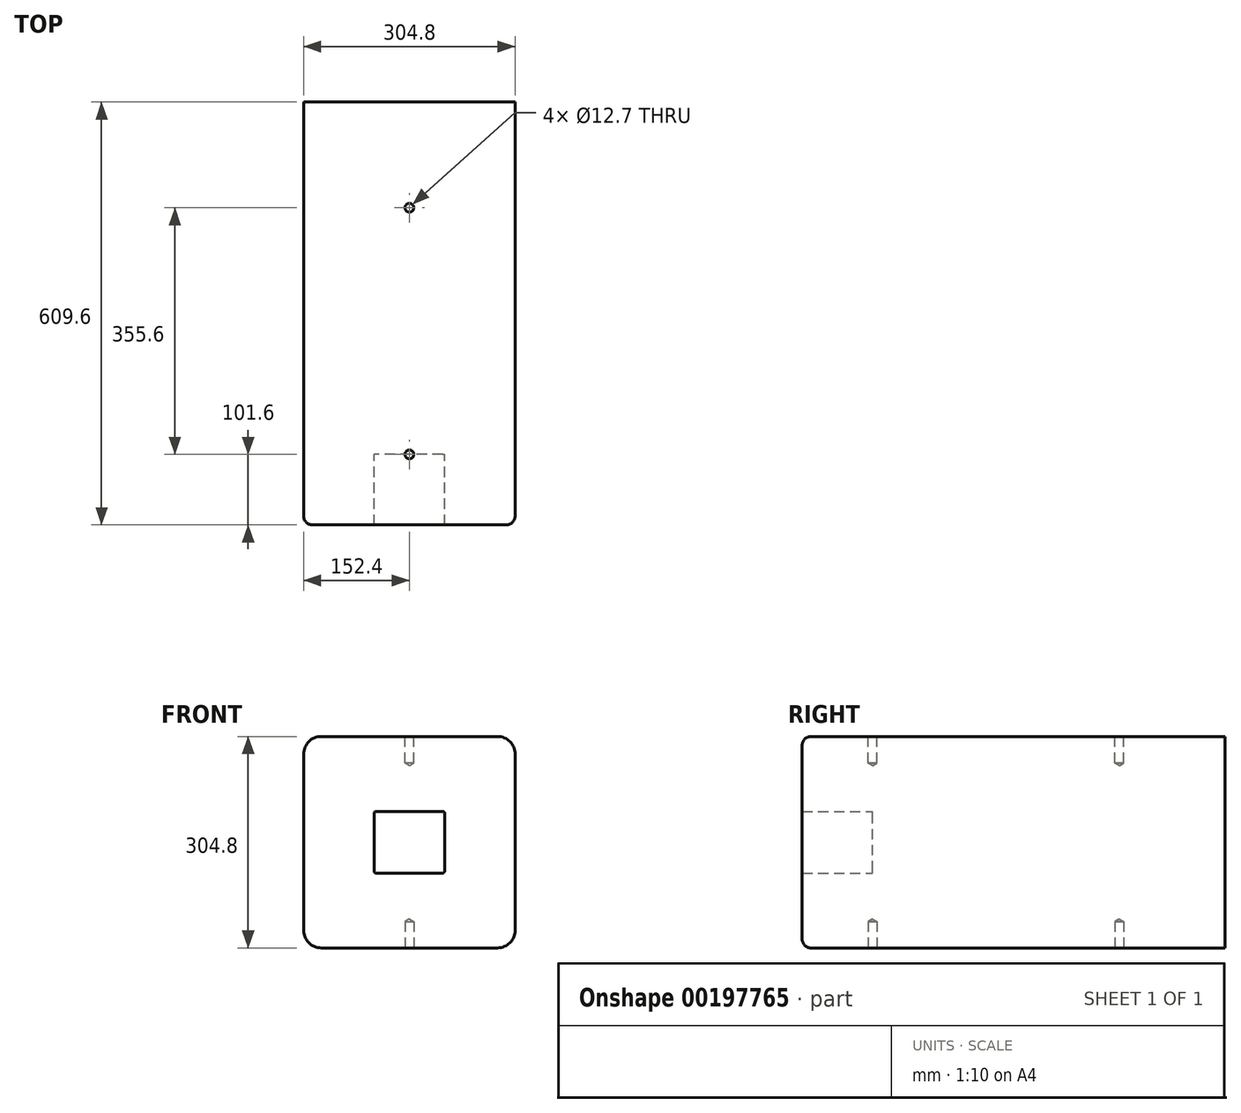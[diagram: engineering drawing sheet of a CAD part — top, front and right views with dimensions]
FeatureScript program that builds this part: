
annotation { "Feature Type Name" : "Feature", "Feature Type Description" : "" }
export const myFeature = defineFeature(function(context is Context, id is Id, definition is map)
    precondition{}
    {
        {
            var Q0;
            Q0=qCreatedBy(makeId("Front.planeOp"),FACE);
            var sketch = newSketch(context, id + "F0", { "sketchPlane" : qUnion([Q0])});
            skLineSegment(sketch, "E0.bottom", {"start": v(152.4, -152.4) * mm, "end": v(-152.4, -152.4) * mm});
            skLineSegment(sketch, "E0.top", {"start": v(152.4, 152.4) * mm, "end": v(-152.4, 152.4) * mm});
            skLineSegment(sketch, "E0.left", {"start": v(152.4, -152.4) * mm, "end": v(152.4, 152.4) * mm});
            skLineSegment(sketch, "E0.right", {"start": v(-152.4, -152.4) * mm, "end": v(-152.4, 152.4) * mm});
            skPoint(sketch, "E0.middle", {"position": v(0, 0) * mm});
            skLineSegment(sketch, "E1.bottom", {"start": v(50.8, -44.45) * mm, "end": v(-50.8, -44.45) * mm});
            skLineSegment(sketch, "E1.top", {"start": v(50.8, 44.45) * mm, "end": v(-50.8, 44.45) * mm});
            skLineSegment(sketch, "E1.left", {"start": v(50.8, -44.45) * mm, "end": v(50.8, 44.45) * mm});
            skLineSegment(sketch, "E1.right", {"start": v(-50.8, -44.45) * mm, "end": v(-50.8, 44.45) * mm});
            skSolve(sketch);
        }
        {
            var Q0;
            Q0=makeQuery(id+"F0.imprint","IMPRINT",FACE,{"disambiguationData":[TD([[makeQuery(id+"F0.imprint","IMPRINT",EDGE,{"derivedFrom":sQuery(id+"F0.wireOp",EDGE,"E0.bottom")}),-1.0]])]});
            extrude(context, id + "F1", {"entities" : qUnion([Q0]), "depth" : 609.6 * mm});
        }
        {
            var Q0;
            Q0=makeQuery(id+"F0.imprint","IMPRINT",FACE,{"disambiguationData":[TD([[makeQuery(id+"F0.imprint","IMPRINT",EDGE,{"derivedFrom":sQuery(id+"F0.wireOp",EDGE,"E1.bottom")}),-1.0]])]});
            extrude(context, id + "F8", {"entities" : qUnion([Q0]), "operationType" : NewBodyOperationType.ADD, "depth" : 508 * mm});
        }
        {
            var Q0;
            Q0=makeQuery(id+"F1.opExtrude","SWEPT_EDGE",EDGE,{"disambiguationData":[OSD([sQuery(id+"F0.wireOp",EDGE,"E0.bottom"),sQuery(id+"F0.wireOp",EDGE,"E0.left")])]});
            var Q1;
            Q1=makeQuery(id+"F1.opExtrude","SWEPT_EDGE",EDGE,{"disambiguationData":[OSD([sQuery(id+"F0.wireOp",EDGE,"E0.bottom"),sQuery(id+"F0.wireOp",EDGE,"E0.right")])]});
            var Q2;
            Q2=makeQuery(id+"F1.opExtrude","SWEPT_EDGE",EDGE,{"disambiguationData":[OSD([sQuery(id+"F0.wireOp",EDGE,"E0.top"),sQuery(id+"F0.wireOp",EDGE,"E0.right")])]});
            var Q3;
            Q3=makeQuery(id+"F1.opExtrude","SWEPT_EDGE",EDGE,{"disambiguationData":[OSD([sQuery(id+"F0.wireOp",EDGE,"E0.top"),sQuery(id+"F0.wireOp",EDGE,"E0.left")])]});
            fillet(context, id + "F2", {"entities" : qUnion([Q0, Q1, Q2, Q3]), "radius" : 25.4 * mm, "tangentPropagation" : true, "allowEdgeOverflow" : false});
        }
        {
            var Q0;
            Q0=makeQuery(id+"F1.opExtrude","CAP_EDGE",EDGE,{"disambiguationData":[OSD([sQuery(id+"F0.wireOp",EDGE,"E0.left")])],"isStart":false});
            fillet(context, id + "F3", {"entities" : qUnion([Q0]), "radius" : 12.7 * mm, "tangentPropagation" : true, "allowEdgeOverflow" : false});
        }
        {
            var Q0;
            Q0=makeQuery(id+"F1.opExtrude","SWEPT_FACE",FACE,{"disambiguationData":[OSD([sQuery(id+"F0.wireOp",EDGE,"E0.bottom")])]});
            var sketch = newSketch(context, id + "F9", { "sketchPlane" : qUnion([Q0])});
            skPoint(sketch, "E2", {"position": v(0, 0) * mm});
            skPoint(sketch, "E3", {"position": v(0, 152.4) * mm});
            skPoint(sketch, "E4", {"position": v(0, 508) * mm});
            skSolve(sketch);
        }
        {
            var Q0;
            Q0=sQuery(id+"FpfZt8s9zI03aznb0_1.wireOp",VERTEX,"6b9960f5-dcf9-4adb-bb65-0d5daa5a9736");
            var Q1;
            Q1=sQuery(id+"FpfZt8s9zI03aznb0_1.wireOp",VERTEX,"4ad32f72-85c8-4d14-baba-c91a9788c939");
            var Q2;
            Q2=sQuery(id+"F9.wireOp",VERTEX,"E3");
            var Q3;
            Q3=sQuery(id+"F9.wireOp",VERTEX,"E4");
            var Q4;
            Q4=makeQuery(id+"F1.opExtrude","SWEPT_BODY",BODY,{"disambiguationData":[OSD([sQuery(id+"F0.wireOp",EDGE,"E0.bottom"),sQuery(id+"F0.wireOp",EDGE,"E0.top"),sQuery(id+"F0.wireOp",EDGE,"E0.left"),sQuery(id+"F0.wireOp",EDGE,"E0.right"),sQuery(id+"F0.wireOp",EDGE,"E1.bottom"),sQuery(id+"F0.wireOp",EDGE,"E1.top"),sQuery(id+"F0.wireOp",EDGE,"E1.left"),sQuery(id+"F0.wireOp",EDGE,"E1.right")])]});
            hole(context, id + "F4", {"style" : HoleStyle.SIMPLE, "endStyle" : HoleEndStyle.BLIND, "holeDiameter" : 12.7 * mm, "holeDepth" : 38.1 * mm, "locations" : qUnion([Q0, Q1, Q2, Q3]), "scope" : qUnion([Q4])});
        }
        {
            var Q0;
            Q0=makeQuery(id+"F1.opExtrude","SWEPT_FACE",FACE,{"disambiguationData":[OSD([sQuery(id+"F0.wireOp",EDGE,"E0.top")])]});
            var sketch = newSketch(context, id + "F5", { "sketchPlane" : qUnion([Q0])});
            skPoint(sketch, "E5", {"position": v(0, -152.4) * mm});
            skPoint(sketch, "E6", {"position": v(0, 0) * mm});
            skPoint(sketch, "E7", {"position": v(0, -508) * mm});
            skSolve(sketch);
        }
        {
            var Q0;
            Q0=sQuery(id+"F5.wireOp",VERTEX,"E7");
            var Q1;
            Q1=sQuery(id+"F5.wireOp",VERTEX,"E5");
            var Q2;
            Q2=makeQuery(id+"F1.opExtrude","SWEPT_BODY",BODY,{"disambiguationData":[OSD([sQuery(id+"F0.wireOp",EDGE,"E0.bottom"),sQuery(id+"F0.wireOp",EDGE,"E0.top"),sQuery(id+"F0.wireOp",EDGE,"E0.left"),sQuery(id+"F0.wireOp",EDGE,"E0.right"),sQuery(id+"F0.wireOp",EDGE,"E1.bottom"),sQuery(id+"F0.wireOp",EDGE,"E1.top"),sQuery(id+"F0.wireOp",EDGE,"E1.left"),sQuery(id+"F0.wireOp",EDGE,"E1.right")])]});
            hole(context, id + "F6", {"style" : HoleStyle.SIMPLE, "endStyle" : HoleEndStyle.BLIND, "holeDiameter" : 12.7 * mm, "holeDepth" : 38.1 * mm, "locations" : qUnion([Q0, Q1]), "scope" : qUnion([Q2])});
        }
        {
            var Q0;
            Q0=makeQuery(id+"F1.opExtrude","SWEPT_EDGE",EDGE,{"disambiguationData":[OSD([sQuery(id+"F0.wireOp",EDGE,"E1.bottom"),sQuery(id+"F0.wireOp",EDGE,"E1.right")])]});
            var Q1;
            Q1=makeQuery(id+"F1.opExtrude","SWEPT_EDGE",EDGE,{"disambiguationData":[OSD([sQuery(id+"F0.wireOp",EDGE,"E1.top"),sQuery(id+"F0.wireOp",EDGE,"E1.right")])]});
            var Q2;
            Q2=makeQuery(id+"F1.opExtrude","SWEPT_EDGE",EDGE,{"disambiguationData":[OSD([sQuery(id+"F0.wireOp",EDGE,"E1.top"),sQuery(id+"F0.wireOp",EDGE,"E1.left")])]});
            var Q3;
            Q3=makeQuery(id+"F1.opExtrude","SWEPT_EDGE",EDGE,{"disambiguationData":[OSD([sQuery(id+"F0.wireOp",EDGE,"E1.bottom"),sQuery(id+"F0.wireOp",EDGE,"E1.left")])]});
            var Q4;
            Q4=makeQuery(id+"F8.opExtrude","CAP_EDGE",EDGE,{"disambiguationData":[OSD([sQuery(id+"F0.wireOp",EDGE,"E1.left")])],"isStart":false});
            var Q5;
            Q5=makeQuery(id+"F8.opExtrude","CAP_EDGE",EDGE,{"disambiguationData":[OSD([sQuery(id+"F0.wireOp",EDGE,"E1.top")])],"isStart":false});
            var Q6;
            Q6=makeQuery(id+"F8.opExtrude","CAP_EDGE",EDGE,{"disambiguationData":[OSD([sQuery(id+"F0.wireOp",EDGE,"E1.right")])],"isStart":false});
            var Q7;
            Q7=makeQuery(id+"F8.opExtrude","CAP_EDGE",EDGE,{"disambiguationData":[OSD([sQuery(id+"F0.wireOp",EDGE,"E1.bottom")])],"isStart":false});
            fillet(context, id + "F7", {"entities" : qUnion([Q0, Q1, Q2, Q3, Q4, Q5, Q6, Q7]), "radius" : 2.54 * mm, "tangentPropagation" : true, "allowEdgeOverflow" : false});
        }
    });
